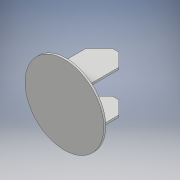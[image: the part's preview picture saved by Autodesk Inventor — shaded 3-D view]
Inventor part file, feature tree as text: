
AUTODESK INVENTOR PART (.ipt)
format: ipt  version: 2018 (Build 220112000, 112)  size: 120,320 bytes
history: native  units: mm
features: extrude x2, sketch x2, chamfer x1
ambient origin geometry x8: Origin, YZ Plane, XZ Plane, XY Plane, X Axis, Y Axis, Z Axis, Center Point
bodies: Solide1 (feature_tree)
feature tree (5):
  extrude  "Extrusion1"  Depth=120.0mm
  extrude  "Extrusion2"  Depth=3.0mm TaperAngle=0.0deg
  chamfer  "Chanfrein1"  Distance=50.0mm
  sketch  "Esquisse1"
  sketch  "Esquisse2"
